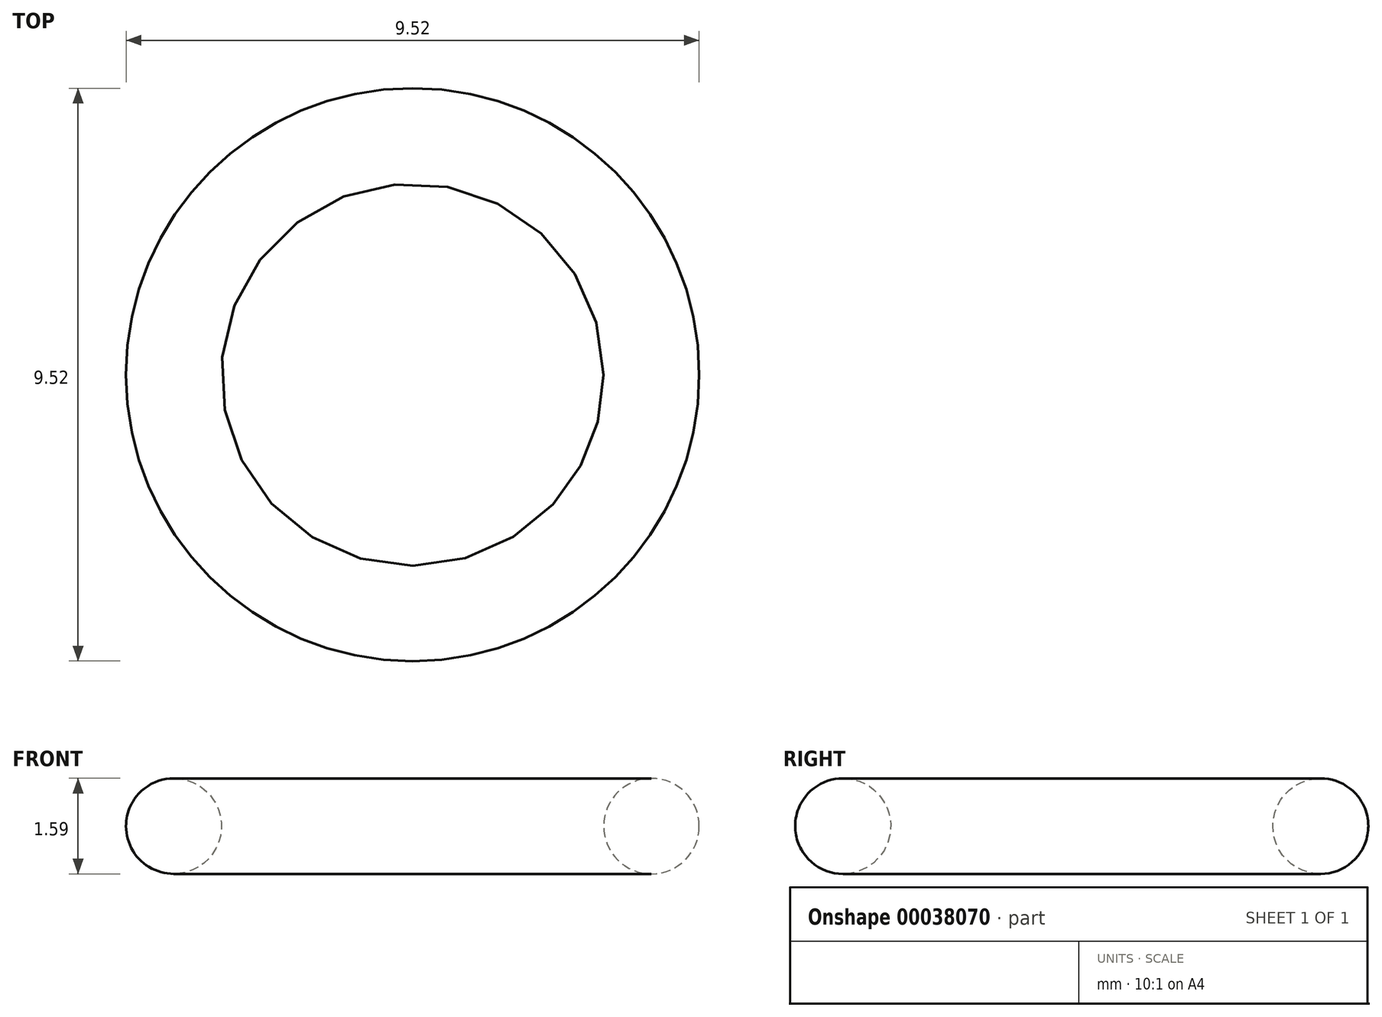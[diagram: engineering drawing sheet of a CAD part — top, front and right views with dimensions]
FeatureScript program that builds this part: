
annotation { "Feature Type Name" : "Feature", "Feature Type Description" : "" }
export const myFeature = defineFeature(function(context is Context, id is Id, definition is map)
    precondition{}
    {
        {
            var Q0;
            Q0=qCreatedBy(makeId("Top.planeOp"),FACE);
            var sketch = newSketch(context, id + "F0", { "sketchPlane" : qUnion([Q0])});
            skCircle(sketch, "E0", {"center": v(0, 0) * mm, "radius": 4.76 * mm});
            skCircle(sketch, "E1", {"center": v(0, 0) * mm, "radius": 3.18 * mm});
            skSolve(sketch);
        }
        {
            var Q0;
            Q0 = qSketchRegion(id + "F0", true);
            extrude(context, id + "F1", {"entities" : qUnion([Q0]), "depth" : 1.59 * mm});
        }
        {
            var Q0;
            Q0=makeQuery(id+"F1.opExtrude","CAP_EDGE",EDGE,{"disambiguationData":[OSD([sQuery(id+"F0.wireOp",EDGE,"E1")])],"isStart":false});
            var Q1;
            Q1=makeQuery(id+"F1.opExtrude","CAP_EDGE",EDGE,{"disambiguationData":[OSD([sQuery(id+"F0.wireOp",EDGE,"E1")])],"isStart":true});
            var Q2;
            Q2=makeQuery(id+"F1.opExtrude","CAP_EDGE",EDGE,{"disambiguationData":[OSD([sQuery(id+"F0.wireOp",EDGE,"E0")])],"isStart":false});
            var Q3;
            Q3=makeQuery(id+"F1.opExtrude","CAP_EDGE",EDGE,{"disambiguationData":[OSD([sQuery(id+"F0.wireOp",EDGE,"E0")])],"isStart":true});
            fillet(context, id + "F2", {"entities" : qUnion([Q0, Q1, Q2, Q3]), "radius" : 0.8 * mm, "tangentPropagation" : true, "allowEdgeOverflow" : false});
        }
    });
